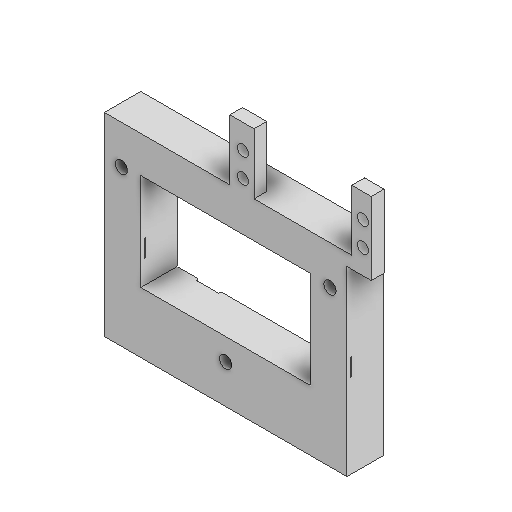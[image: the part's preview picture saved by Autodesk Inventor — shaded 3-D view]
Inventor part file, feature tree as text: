
AUTODESK INVENTOR PART (.ipt)
format: ipt  version: 2025.1 (Build 291241000, 241)  size: 236,032 bytes
history: native  units: mm
features: sketch x10, extrude x8, hole x2, chamfer x1
ambient origin geometry x8: Origin, YZ Plane, XZ Plane, XY Plane, X Axis, Y Axis, Z Axis, Center Point
bodies: Body1 (feature_tree)
feature tree (21):
  extrude  "Wyciągnięcie proste4"  Depth=100.0mm
  extrude  "Wyciągnięcie proste5"  Depth=80.0mm
  extrude  "Wyciągnięcie proste6"  Depth=70.0mm
  extrude  "Wyciągnięcie proste7"  Depth=50.0mm
  hole  "Otwór2"  [1 undecoded]
  extrude  "Wyciągnięcie proste8"  Depth=2.0mm TaperAngle=0.0deg
  chamfer  "Faza2"  Distance=0.5mm
  extrude  "Wyciągnięcie proste9"  Depth=7.0mm
  extrude  "Wyciągnięcie proste10"  Depth=1.5mm
  extrude  "Wyciągnięcie proste11"  Depth=41.741mm
  hole  "Otwór3"  [1 undecoded]
  sketch  "Szkic5"
  sketch  "Szkic6"
  sketch  "Szkic7"
  sketch  "Szkic8"
  sketch  "Szkic9"
  sketch  "Szkic10"
  sketch  "Szkic11"
  sketch  "Szkic12"
  sketch  "Szkic14"
  sketch  "Szkic15"
note: 2 required parameter values undecoded (feature->parameter linkage not recoverable at this tier; creation-order binding heuristic only, values carry confidence <= 0.55)
